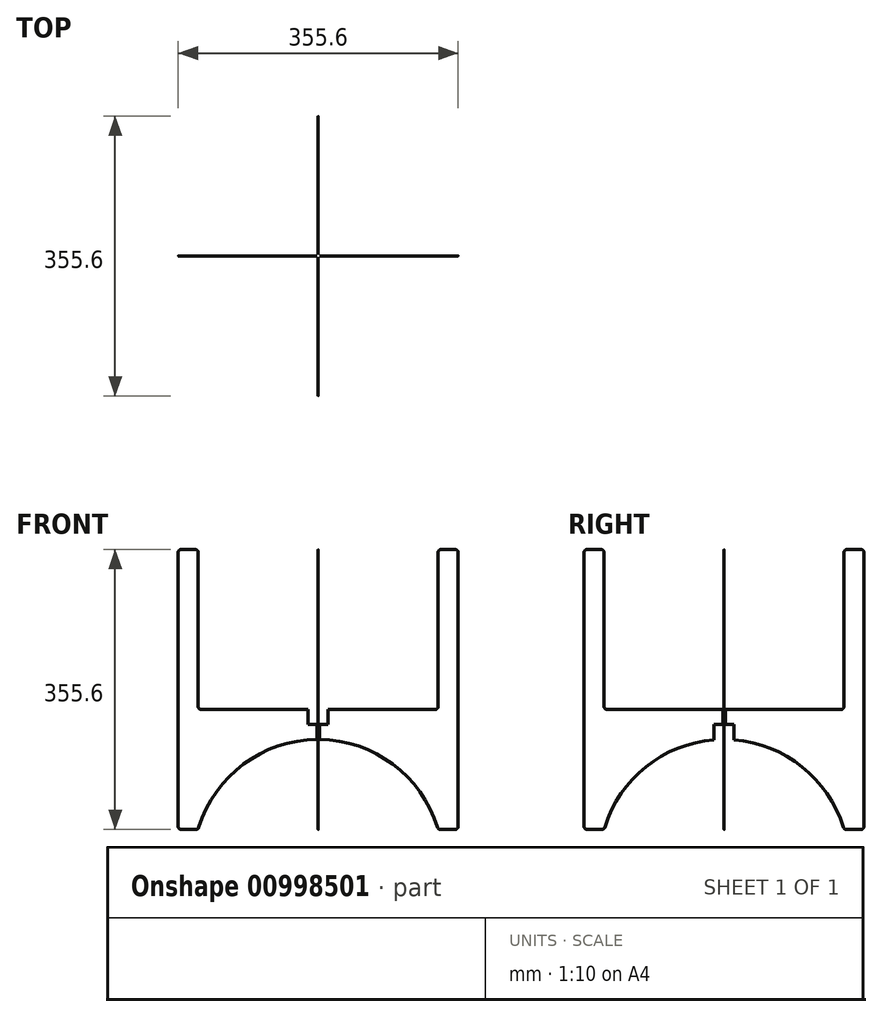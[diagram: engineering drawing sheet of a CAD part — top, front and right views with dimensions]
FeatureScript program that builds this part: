
annotation { "Feature Type Name" : "Feature", "Feature Type Description" : "" }
export const myFeature = defineFeature(function(context is Context, id is Id, definition is map)
    precondition{}
    {
        {
            var Q0;
            Q0=qCreatedBy(makeId("Front.planeOp"),FACE);
            var sketch = newSketch(context, id + "F0", { "sketchPlane" : qUnion([Q0])});
            skArc(sketch, "E0", {"start": v(0, 0) * mm, "mid": v(-94.13, -30.92) * mm, "end": v(-151.6, -111.62) * mm});
            skLineSegment(sketch, "E1", {"start": v(-155.23, -114.3) * mm, "end": v(-173.99, -114.3) * mm});
            skLineSegment(sketch, "E2", {"start": v(-177.8, -110.5) * mm, "end": v(-177.8, 237.49) * mm});
            skLineSegment(sketch, "E3", {"start": v(-173.99, 241.3) * mm, "end": v(-156.21, 241.3) * mm});
            skLineSegment(sketch, "E4", {"start": v(-152.4, 237.49) * mm, "end": v(-152.4, 41.9) * mm});
            skLineSegment(sketch, "E5", {"start": v(-148.6, 38.1) * mm, "end": v(0, 38.1) * mm});
            skLineSegment(sketch, "E6", {"start": v(0, 38.1) * mm, "end": v(0, 0) * mm, "construction": true});
            skPoint(sketch, "E7.orphan", {"position": v(152.4, -114.3) * mm});
            skArc(sketch, "E8.MirrorCS", {"start": v(0, 0) * mm, "mid": v(94.13, -30.92) * mm, "end": v(151.6, -111.62) * mm});
            skLineSegment(sketch, "E9.MirrorCS", {"start": v(155.23, -114.3) * mm, "end": v(174, -114.3) * mm});
            skLineSegment(sketch, "E10.MirrorCS", {"start": v(177.8, -110.5) * mm, "end": v(177.8, 237.5) * mm});
            skLineSegment(sketch, "E11.MirrorCS", {"start": v(173.99, 241.3) * mm, "end": v(156.2, 241.3) * mm});
            skLineSegment(sketch, "E12.MirrorCS", {"start": v(152.4, 237.49) * mm, "end": v(152.4, 41.9) * mm});
            skLineSegment(sketch, "E13.MirrorCS", {"start": v(148.6, 38.1) * mm, "end": v(0, 38.1) * mm});
            skPoint(sketch, "E14.visualSharp", {"position": v(-177.8, 241.3) * mm});
            skArc(sketch, "E14.filletArc", {"start": v(-173.99, 241.3) * mm, "mid": v(-176.68, 240.18) * mm, "end": v(-177.8, 237.49) * mm});
            skPoint(sketch, "E15.visualSharp", {"position": v(-152.4, 38.1) * mm});
            skArc(sketch, "E15.filletArc", {"start": v(-152.4, 41.9) * mm, "mid": v(-151.28, 39.22) * mm, "end": v(-148.6, 38.1) * mm});
            skPoint(sketch, "E16.visualSharp", {"position": v(152.4, 241.3) * mm});
            skArc(sketch, "E16.filletArc", {"start": v(156.2, 241.3) * mm, "mid": v(153.52, 240.18) * mm, "end": v(152.4, 237.49) * mm});
            skPoint(sketch, "E17.visualSharp", {"position": v(177.8, 241.3) * mm});
            skArc(sketch, "E17.filletArc", {"start": v(177.8, 237.5) * mm, "mid": v(176.68, 240.18) * mm, "end": v(173.99, 241.3) * mm});
            skPoint(sketch, "E18.visualSharp", {"position": v(-177.8, -114.3) * mm});
            skArc(sketch, "E18.filletArc", {"start": v(-177.8, -110.5) * mm, "mid": v(-176.68, -113.18) * mm, "end": v(-173.99, -114.3) * mm});
            skArc(sketch, "E19.filletArc", {"start": v(151.6, -111.62) * mm, "mid": v(152.97, -113.56) * mm, "end": v(155.23, -114.3) * mm});
            skPoint(sketch, "E20.visualSharp", {"position": v(-152.4, -114.3) * mm});
            skArc(sketch, "E20.filletArc", {"start": v(-155.23, -114.3) * mm, "mid": v(-152.97, -113.56) * mm, "end": v(-151.6, -111.62) * mm});
            skPoint(sketch, "E21.visualSharp", {"position": v(177.8, -114.3) * mm});
            skArc(sketch, "E21.filletArc", {"start": v(174, -114.3) * mm, "mid": v(176.68, -113.18) * mm, "end": v(177.8, -110.5) * mm});
            skPoint(sketch, "E22.visualSharp", {"position": v(152.4, 38.1) * mm});
            skArc(sketch, "E22.filletArc", {"start": v(148.6, 38.1) * mm, "mid": v(151.28, 39.22) * mm, "end": v(152.4, 41.9) * mm});
            skPoint(sketch, "E23.visualSharp", {"position": v(-152.4, 241.3) * mm});
            skArc(sketch, "E23.filletArc", {"start": v(-152.4, 237.49) * mm, "mid": v(-153.52, 240.18) * mm, "end": v(-156.21, 241.3) * mm});
            skSolve(sketch);
        }
        {
            var Q0;
            Q0 = qSketchRegion(id + "F0", true);
            extrude(context, id + "F1", {"entities" : qUnion([Q0]), "depth" : .125 / 50.8 * mm, "offsetDistance" : 25.4 * mm});
        }
        {
            var Q0;
            Q0=makeQuery(id+"F1.opExtrude","SWEPT_BODY",BODY,{"disambiguationData":[OSD([sQuery(id+"F0.wireOp",EDGE,"E0"),sQuery(id+"F0.wireOp",EDGE,"E1"),sQuery(id+"F0.wireOp",EDGE,"E2"),sQuery(id+"F0.wireOp",EDGE,"E3"),sQuery(id+"F0.wireOp",EDGE,"E4"),sQuery(id+"F0.wireOp",EDGE,"E5"),sQuery(id+"F0.wireOp",EDGE,"E8.MirrorCS"),sQuery(id+"F0.wireOp",EDGE,"E9.MirrorCS"),sQuery(id+"F0.wireOp",EDGE,"E10.MirrorCS"),sQuery(id+"F0.wireOp",EDGE,"E11.MirrorCS"),sQuery(id+"F0.wireOp",EDGE,"E12.MirrorCS"),sQuery(id+"F0.wireOp",EDGE,"E13.MirrorCS"),sQuery(id+"F0.wireOp",EDGE,"E14.filletArc"),sQuery(id+"F0.wireOp",EDGE,"E15.filletArc"),sQuery(id+"F0.wireOp",EDGE,"E16.filletArc"),sQuery(id+"F0.wireOp",EDGE,"E17.filletArc"),sQuery(id+"F0.wireOp",EDGE,"E18.filletArc"),sQuery(id+"F0.wireOp",EDGE,"E19.filletArc"),sQuery(id+"F0.wireOp",EDGE,"E20.filletArc"),sQuery(id+"F0.wireOp",EDGE,"E21.filletArc"),sQuery(id+"F0.wireOp",EDGE,"E22.filletArc"),sQuery(id+"F0.wireOp",EDGE,"E23.filletArc")])]});
            var Q1;
            Q1=sQuery(id+"F0.wireOp",EDGE,"E6");
            circularPattern(context, id + "F2", {"entities" : qUnion([Q0]), "axis" : qUnion([Q1]), "angle" : 360 * degree, "instanceCount" : 4, "equalSpace" : true, "isCentered" : true});
        }
        {
            var Q0;
            Q0=makeQuery(id+"F2.opPattern","COPY",BODY,{"derivedFrom":makeQuery(id+"F1.opExtrude","SWEPT_BODY",BODY,{"disambiguationData":[OSD([sQuery(id+"F0.wireOp",EDGE,"E0"),sQuery(id+"F0.wireOp",EDGE,"E1"),sQuery(id+"F0.wireOp",EDGE,"E2"),sQuery(id+"F0.wireOp",EDGE,"E3"),sQuery(id+"F0.wireOp",EDGE,"E4"),sQuery(id+"F0.wireOp",EDGE,"E5"),sQuery(id+"F0.wireOp",EDGE,"E8.MirrorCS"),sQuery(id+"F0.wireOp",EDGE,"E9.MirrorCS"),sQuery(id+"F0.wireOp",EDGE,"E10.MirrorCS"),sQuery(id+"F0.wireOp",EDGE,"E11.MirrorCS"),sQuery(id+"F0.wireOp",EDGE,"E12.MirrorCS"),sQuery(id+"F0.wireOp",EDGE,"E13.MirrorCS"),sQuery(id+"F0.wireOp",EDGE,"E14.filletArc"),sQuery(id+"F0.wireOp",EDGE,"E15.filletArc"),sQuery(id+"F0.wireOp",EDGE,"E16.filletArc"),sQuery(id+"F0.wireOp",EDGE,"E17.filletArc"),sQuery(id+"F0.wireOp",EDGE,"E18.filletArc"),sQuery(id+"F0.wireOp",EDGE,"E19.filletArc"),sQuery(id+"F0.wireOp",EDGE,"E20.filletArc"),sQuery(id+"F0.wireOp",EDGE,"E21.filletArc"),sQuery(id+"F0.wireOp",EDGE,"E22.filletArc"),sQuery(id+"F0.wireOp",EDGE,"E23.filletArc")])]}),"instanceName":"1"});
            deleteBodies(context, id + "F3", {"entities" : qUnion([Q0])});
        }
        {
            var Q0;
            Q0=makeQuery(id+"F2.opPattern","COPY",FACE,{"derivedFrom":makeQuery(id+"F1.opExtrude","CAP_FACE",FACE,{"disambiguationData":[OSD([sQuery(id+"F0.wireOp",EDGE,"E0"),sQuery(id+"F0.wireOp",EDGE,"E1"),sQuery(id+"F0.wireOp",EDGE,"E2"),sQuery(id+"F0.wireOp",EDGE,"E3"),sQuery(id+"F0.wireOp",EDGE,"E4"),sQuery(id+"F0.wireOp",EDGE,"E5"),sQuery(id+"F0.wireOp",EDGE,"E8.MirrorCS"),sQuery(id+"F0.wireOp",EDGE,"E9.MirrorCS"),sQuery(id+"F0.wireOp",EDGE,"E10.MirrorCS"),sQuery(id+"F0.wireOp",EDGE,"E11.MirrorCS"),sQuery(id+"F0.wireOp",EDGE,"E12.MirrorCS"),sQuery(id+"F0.wireOp",EDGE,"E13.MirrorCS"),sQuery(id+"F0.wireOp",EDGE,"E14.filletArc"),sQuery(id+"F0.wireOp",EDGE,"E15.filletArc"),sQuery(id+"F0.wireOp",EDGE,"E16.filletArc"),sQuery(id+"F0.wireOp",EDGE,"E17.filletArc"),sQuery(id+"F0.wireOp",EDGE,"E18.filletArc"),sQuery(id+"F0.wireOp",EDGE,"E19.filletArc"),sQuery(id+"F0.wireOp",EDGE,"E20.filletArc"),sQuery(id+"F0.wireOp",EDGE,"E21.filletArc"),sQuery(id+"F0.wireOp",EDGE,"E22.filletArc"),sQuery(id+"F0.wireOp",EDGE,"E23.filletArc")])],"isStart":false}),"instanceName":"-1"});
            var sketch = newSketch(context, id + "F4", { "sketchPlane" : qUnion([Q0])});
            skLineSegment(sketch, "E24.bottom", {"start": v(-1.59, 38.1) * mm, "end": v(1.59, 38.1) * mm});
            skLineSegment(sketch, "E24.top", {"start": v(-1.59, 19.05) * mm, "end": v(1.59, 19.05) * mm});
            skLineSegment(sketch, "E24.left", {"start": v(-1.59, 38.1) * mm, "end": v(-1.59, 19.05) * mm});
            skLineSegment(sketch, "E24.right", {"start": v(1.59, 38.1) * mm, "end": v(1.59, 19.05) * mm});
            skLineSegment(sketch, "E25", {"start": v(0, 19.05) * mm, "end": v(0, 38.1) * mm, "construction": true});
            skPoint(sketch, "E25.startSnap0", {"position": v(0, 38.1) * mm});
            skSolve(sketch);
        }
        {
            var Q0;
            Q0 = qSketchRegion(id + "F4", true);
            extrude(context, id + "F5", {"entities" : qUnion([Q0]), "operationType" : NewBodyOperationType.REMOVE, "endBound" : BoundingType.SYMMETRIC, "oppositeDirection" : true, "depth" : 25.4 * mm, "offsetDistance" : 25.4 * mm});
        }
        {
            var Q0;
            Q0=makeQuery(id+"F1.opExtrude","CAP_FACE",FACE,{"disambiguationData":[OSD([sQuery(id+"F0.wireOp",EDGE,"E0"),sQuery(id+"F0.wireOp",EDGE,"E1"),sQuery(id+"F0.wireOp",EDGE,"E2"),sQuery(id+"F0.wireOp",EDGE,"E3"),sQuery(id+"F0.wireOp",EDGE,"E4"),sQuery(id+"F0.wireOp",EDGE,"E5"),sQuery(id+"F0.wireOp",EDGE,"E8.MirrorCS"),sQuery(id+"F0.wireOp",EDGE,"E9.MirrorCS"),sQuery(id+"F0.wireOp",EDGE,"E10.MirrorCS"),sQuery(id+"F0.wireOp",EDGE,"E11.MirrorCS"),sQuery(id+"F0.wireOp",EDGE,"E12.MirrorCS"),sQuery(id+"F0.wireOp",EDGE,"E13.MirrorCS"),sQuery(id+"F0.wireOp",EDGE,"E14.filletArc"),sQuery(id+"F0.wireOp",EDGE,"E15.filletArc"),sQuery(id+"F0.wireOp",EDGE,"E16.filletArc"),sQuery(id+"F0.wireOp",EDGE,"E17.filletArc"),sQuery(id+"F0.wireOp",EDGE,"E18.filletArc"),sQuery(id+"F0.wireOp",EDGE,"E19.filletArc"),sQuery(id+"F0.wireOp",EDGE,"E20.filletArc"),sQuery(id+"F0.wireOp",EDGE,"E21.filletArc"),sQuery(id+"F0.wireOp",EDGE,"E22.filletArc"),sQuery(id+"F0.wireOp",EDGE,"E23.filletArc")])],"isStart":false});
            var sketch = newSketch(context, id + "F6", { "sketchPlane" : qUnion([Q0])});
            skLineSegment(sketch, "E26.bottom", {"start": v(-1.59, 19.05) * mm, "end": v(1.59, 19.05) * mm});
            skLineSegment(sketch, "E26.top", {"start": v(-1.59, -11.43) * mm, "end": v(1.59, -11.43) * mm});
            skLineSegment(sketch, "E26.left", {"start": v(-1.59, 19.05) * mm, "end": v(-1.59, -11.43) * mm});
            skLineSegment(sketch, "E26.right", {"start": v(1.59, 19.05) * mm, "end": v(1.59, -11.43) * mm});
            skLineSegment(sketch, "E27.bottom", {"start": v(0, 19.05) * mm, "end": v(0, 19.05) * mm});
            skLineSegment(sketch, "E27.top", {"start": v(0, -11.43) * mm, "end": v(0, -11.43) * mm});
            skLineSegment(sketch, "E27.left", {"start": v(0, 19.05) * mm, "end": v(0, -11.43) * mm, "construction": true});
            skLineSegment(sketch, "E27.right", {"start": v(0, 19.05) * mm, "end": v(0, -11.43) * mm, "construction": true});
            skSolve(sketch);
        }
        {
            var Q0;
            Q0 = qSketchRegion(id + "F6", true);
            extrude(context, id + "F7", {"entities" : qUnion([Q0]), "operationType" : NewBodyOperationType.REMOVE, "endBound" : BoundingType.SYMMETRIC, "oppositeDirection" : true, "depth" : 25.4 * mm, "offsetDistance" : 25.4 * mm});
        }
    });
